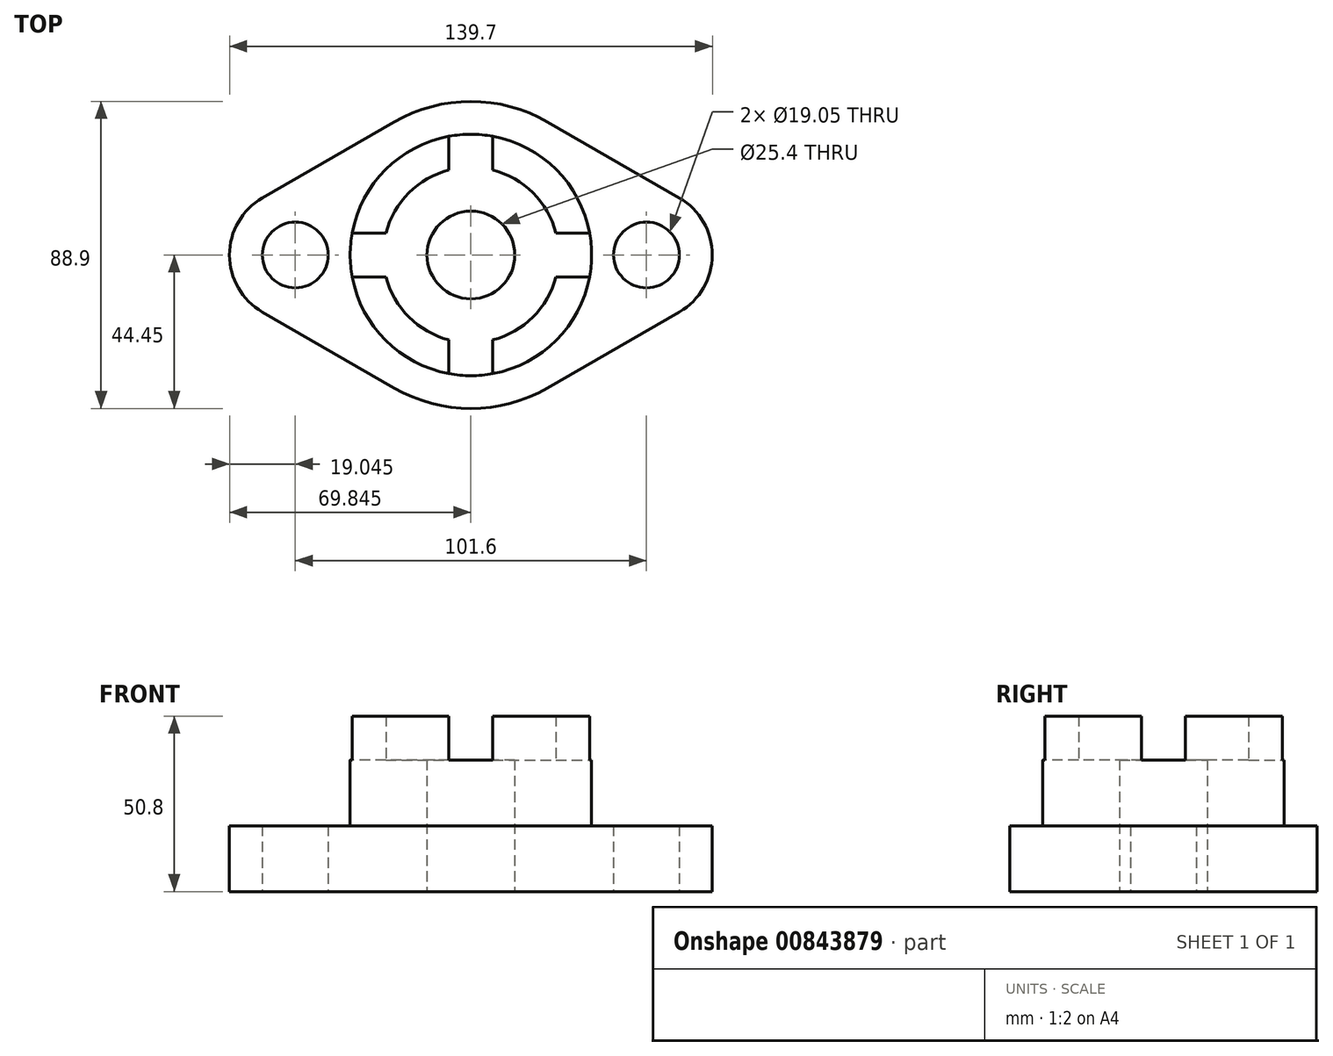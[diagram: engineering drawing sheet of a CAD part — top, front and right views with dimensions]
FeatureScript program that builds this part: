
annotation { "Feature Type Name" : "Feature", "Feature Type Description" : "" }
export const myFeature = defineFeature(function(context is Context, id is Id, definition is map)
    precondition{}
    {
        {
            var Q0;
            Q0=qCreatedBy(makeId("Top.planeOp"),FACE);
            var sketch = newSketch(context, id + "F0", { "sketchPlane" : qUnion([Q0])});
            skCircle(sketch, "E0", {"center": v(-27.9, 0) * mm, "radius": 9.53 * mm});
            skCircle(sketch, "E1", {"center": v(73.7, 0) * mm, "radius": 9.53 * mm});
            skArc(sketch, "E2", {"start": v(0.68, -38.5) * mm, "mid": v(22.9, -44.45) * mm, "end": v(45.13, -38.5) * mm});
            skArc(sketch, "E3", {"start": v(-37.42, 16.5) * mm, "mid": v(-46.94, 0) * mm, "end": v(-37.42, -16.5) * mm});
            skArc(sketch, "E4", {"start": v(83.23, -16.5) * mm, "mid": v(92.76, 0) * mm, "end": v(83.23, 16.5) * mm});
            skLineSegment(sketch, "E5", {"start": v(-37.42, 16.5) * mm, "end": v(0.68, 38.5) * mm});
            skLineSegment(sketch, "E6", {"start": v(-37.42, -16.5) * mm, "end": v(0.68, -38.5) * mm});
            skLineSegment(sketch, "E7", {"start": v(45.13, -38.5) * mm, "end": v(83.23, -16.5) * mm});
            skLineSegment(sketch, "E8", {"start": v(45.13, 38.5) * mm, "end": v(83.23, 16.5) * mm});
            skArc(sketch, "E9.trimOffspring", {"start": v(45.13, 38.5) * mm, "mid": v(22.9, 44.45) * mm, "end": v(0.68, 38.5) * mm});
            skCircle(sketch, "E10", {"center": v(22.9, 0) * mm, "radius": 12.7 * mm});
            skSolve(sketch);
        }
        {
            var Q0;
            Q0 = qSketchRegion(id + "F0", true);
            extrude(context, id + "F1", {"entities" : qUnion([Q0]), "depth" : 19.05 * mm, "offsetDistance" : 25.4 * mm});
        }
        {
            var Q0;
            Q0=makeQuery(id+"F1.opExtrude","CAP_FACE",FACE,{"disambiguationData":[OSD([sQuery(id+"F0.wireOp",EDGE,"E0"),sQuery(id+"F0.wireOp",EDGE,"E1"),sQuery(id+"F0.wireOp",EDGE,"E2"),sQuery(id+"F0.wireOp",EDGE,"E3"),sQuery(id+"F0.wireOp",EDGE,"E4"),sQuery(id+"F0.wireOp",EDGE,"E5"),sQuery(id+"F0.wireOp",EDGE,"E6"),sQuery(id+"F0.wireOp",EDGE,"E7"),sQuery(id+"F0.wireOp",EDGE,"E8"),sQuery(id+"F0.wireOp",EDGE,"E9.trimOffspring")])],"isStart":false});
            var sketch = newSketch(context, id + "F2", { "sketchPlane" : qUnion([Q0])});
            skCircle(sketch, "E11", {"center": v(22.9, 0) * mm, "radius": 34.93 * mm});
            skPoint(sketch, "E12.orphan", {"position": v(22.9, -44.45) * mm});
            skPoint(sketch, "E13.orphan", {"position": v(92.76, 0) * mm});
            skPoint(sketch, "E14.orphan", {"position": v(-46.94, 0) * mm});
            skPoint(sketch, "E15.orphan", {"position": v(22.9, 44.45) * mm});
            skCircle(sketch, "E16", {"center": v(22.9, 0) * mm, "radius": 12.7 * mm});
            skSolve(sketch);
        }
        {
            var Q0;
            Q0 = qSketchRegion(id + "F2", true);
            extrude(context, id + "F3", {"entities" : qUnion([Q0]), "operationType" : NewBodyOperationType.ADD, "depth" : 19.05 * mm, "offsetDistance" : 25.4 * mm});
        }
        {
            var Q0;
            Q0=makeQuery(id+"F3.opExtrude","CAP_FACE",FACE,{"disambiguationData":[OSD([sQuery(id+"F2.wireOp",EDGE,"E11"),sQuery(id+"F2.wireOp",EDGE,"E16")])],"isStart":false});
            var sketch = newSketch(context, id + "F4", { "sketchPlane" : qUnion([Q0])});
            skArc(sketch, "E17", {"start": v(57.25, 6.35) * mm, "mid": v(47.6, 24.7) * mm, "end": v(29.26, 34.34) * mm});
            skArc(sketch, "E18", {"start": v(47.5, 6.35) * mm, "mid": v(40.87, 17.96) * mm, "end": v(29.26, 24.6) * mm});
            skLineSegment(sketch, "E19", {"start": v(29.26, -30.16) * mm, "end": v(29.26, -24.6) * mm});
            skLineSegment(sketch, "E20", {"start": v(29.26, -24.6) * mm, "end": v(29.26, -34.34) * mm});
            skLineSegment(sketch, "E21", {"start": v(16.56, -30.16) * mm, "end": v(16.56, -24.6) * mm});
            skLineSegment(sketch, "E22", {"start": v(16.56, -24.6) * mm, "end": v(16.56, -34.34) * mm});
            skPoint(sketch, "E23.start.orphan", {"position": v(22.9, -30.16) * mm});
            skPoint(sketch, "E24.orphan", {"position": v(22.9, -25.4) * mm});
            skPoint(sketch, "E25.end.orphan", {"position": v(22.9, -34.93) * mm});
            skLineSegment(sketch, "E26", {"start": v(-7.26, 6.35) * mm, "end": v(-1.69, 6.35) * mm});
            skLineSegment(sketch, "E27", {"start": v(-1.69, 6.35) * mm, "end": v(-11.44, 6.35) * mm});
            skLineSegment(sketch, "E28", {"start": v(-7.26, -6.35) * mm, "end": v(-1.69, -6.35) * mm});
            skLineSegment(sketch, "E29", {"start": v(-1.69, -6.35) * mm, "end": v(-11.44, -6.35) * mm});
            skPoint(sketch, "E30.orphan", {"position": v(-2.5, 0) * mm});
            skPoint(sketch, "E31.end.orphan", {"position": v(-12.02, 0) * mm});
            skPoint(sketch, "E31.start.orphan", {"position": v(-7.26, 0) * mm});
            skLineSegment(sketch, "E32", {"start": v(16.56, 30.16) * mm, "end": v(16.56, 34.34) * mm});
            skLineSegment(sketch, "E33", {"start": v(16.56, 34.34) * mm, "end": v(16.56, 24.6) * mm});
            skLineSegment(sketch, "E34", {"start": v(29.26, 30.16) * mm, "end": v(29.26, 34.34) * mm});
            skLineSegment(sketch, "E35", {"start": v(29.26, 34.34) * mm, "end": v(29.26, 24.6) * mm});
            skPoint(sketch, "E36.orphan", {"position": v(22.9, 34.93) * mm});
            skPoint(sketch, "E37.start.orphan", {"position": v(22.9, 25.4) * mm});
            skPoint(sketch, "E38.start.orphan", {"position": v(22.9, 30.16) * mm});
            skLineSegment(sketch, "E39", {"start": v(53.07, 6.35) * mm, "end": v(47.5, 6.35) * mm});
            skLineSegment(sketch, "E40", {"start": v(47.5, 6.35) * mm, "end": v(57.25, 6.35) * mm});
            skLineSegment(sketch, "E41", {"start": v(53.07, -6.35) * mm, "end": v(57.25, -6.35) * mm});
            skLineSegment(sketch, "E42", {"start": v(57.25, -6.35) * mm, "end": v(47.5, -6.35) * mm});
            skPoint(sketch, "E43.orphan", {"position": v(57.83, 0) * mm});
            skPoint(sketch, "E44.start.orphan", {"position": v(48.3, 0) * mm});
            skPoint(sketch, "E45.end.orphan", {"position": v(53.07, 0) * mm});
            skArc(sketch, "E46.trimOffspring", {"start": v(16.56, 34.34) * mm, "mid": v(-1.8, 24.7) * mm, "end": v(-11.44, 6.35) * mm});
            skArc(sketch, "E47.trimOffspring", {"start": v(16.56, 24.6) * mm, "mid": v(4.94, 17.96) * mm, "end": v(-1.69, 6.35) * mm});
            skArc(sketch, "E48.trimOffspring", {"start": v(-11.44, -6.35) * mm, "mid": v(-1.8, -24.7) * mm, "end": v(16.56, -34.34) * mm});
            skArc(sketch, "E49.trimOffspring", {"start": v(-1.69, -6.35) * mm, "mid": v(4.94, -17.96) * mm, "end": v(16.56, -24.6) * mm});
            skArc(sketch, "E50.trimOffspring", {"start": v(29.26, -34.34) * mm, "mid": v(47.6, -24.7) * mm, "end": v(57.25, -6.35) * mm});
            skArc(sketch, "E51.trimOffspring", {"start": v(29.26, -24.6) * mm, "mid": v(40.87, -17.96) * mm, "end": v(47.5, -6.35) * mm});
            skSolve(sketch);
        }
        {
            var Q0;
            Q0 = qSketchRegion(id + "F4", true);
            extrude(context, id + "F5", {"entities" : qUnion([Q0]), "operationType" : NewBodyOperationType.ADD, "depth" : 12.7 * mm, "offsetDistance" : 25.4 * mm});
        }
    });
